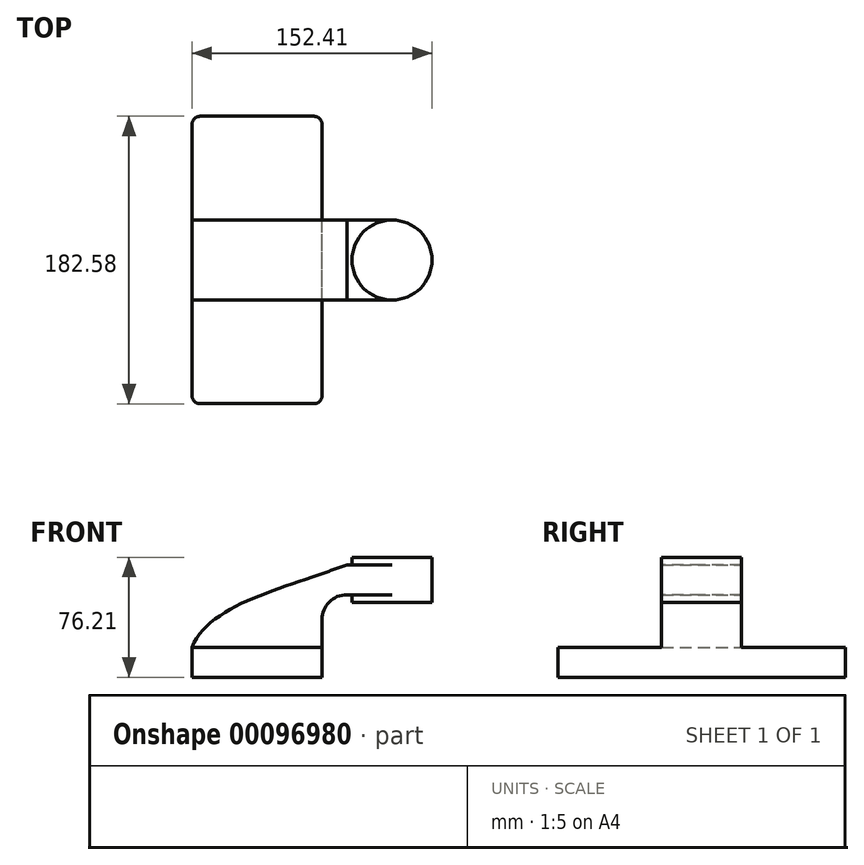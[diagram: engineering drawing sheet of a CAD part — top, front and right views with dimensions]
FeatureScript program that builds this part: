
annotation { "Feature Type Name" : "Feature", "Feature Type Description" : "" }
export const myFeature = defineFeature(function(context is Context, id is Id, definition is map)
    precondition{}
    {
        {
            var Q0;
            Q0=qCreatedBy(makeId("Front.planeOp"),FACE);
            var sketch = newSketch(context, id + "F0", { "sketchPlane" : qUnion([Q0])});
            skLineSegment(sketch, "E0.rect.bottom", {"start": v(-41.28, 9.53) * mm, "end": v(41.28, 9.53) * mm});
            skLineSegment(sketch, "E0.rect.top", {"start": v(-41.28, -9.53) * mm, "end": v(41.28, -9.53) * mm});
            skLineSegment(sketch, "E0.rect.left", {"start": v(-41.28, 9.52) * mm, "end": v(-41.28, -9.52) * mm});
            skLineSegment(sketch, "E0.rect.right", {"start": v(41.28, 9.52) * mm, "end": v(41.28, -9.52) * mm});
            skPoint(sketch, "E0.rect.middle", {"position": v(0, 0) * mm});
            skLineSegment(sketch, "E1", {"start": v(41.28, 9.52) * mm, "end": v(41.28, 27) * mm});
            skArc(sketch, "E2", {"start": v(41.28, 27) * mm, "mid": v(45.92, 38.23) * mm, "end": v(57.15, 42.88) * mm});
            skLineSegment(sketch, "E3", {"start": v(57.15, 42.88) * mm, "end": v(85.72, 42.88) * mm});
            skLineSegment(sketch, "E4.rect.bottom", {"start": v(60.32, 38.1) * mm, "end": v(111.12, 38.1) * mm});
            skLineSegment(sketch, "E4.rect.top", {"start": v(62.86, 66.67) * mm, "end": v(111.12, 66.67) * mm});
            skLineSegment(sketch, "E4.rect.left", {"start": v(60.32, 38.1) * mm, "end": v(60.32, 64.14) * mm});
            skLineSegment(sketch, "E4.rect.right", {"start": v(111.12, 38.1) * mm, "end": v(111.12, 66.68) * mm});
            skPoint(sketch, "E4.rect.middle", {"position": v(85.72, 52.39) * mm});
            skLineSegment(sketch, "E5.0", {"start": v(57.15, 61.93) * mm, "end": v(85.72, 61.93) * mm});
            skArc(sketch, "E5.1", {"start": v(22.23, 27) * mm, "mid": v(32.45, 51.7) * mm, "end": v(57.15, 61.93) * mm});
            skLineSegment(sketch, "E5.2", {"start": v(22.23, 9.53) * mm, "end": v(22.23, 27) * mm});
            skLineSegment(sketch, "E6", {"start": v(85.72, 38.1) * mm, "end": v(85.72, 66.68) * mm});
            skFitSpline(sketch, "E7", {"points": [v(-41.28, 9.52) * mm, v(57.15, 61.93) * mm], "startDerivative": vector(34.3, 84.37) * mm, "endDerivative": vector(112.4, 43.35) * mm});
            skPoint(sketch, "E8.visualSharp", {"position": v(60.32, 66.68) * mm});
            skArc(sketch, "E8.filletArc", {"start": v(62.86, 66.68) * mm, "mid": v(61.07, 65.93) * mm, "end": v(60.32, 64.14) * mm});
            skSolve(sketch);
        }
        {
            var Q0;
            Q0=makeQuery(id+"F0.imprint","IMPRINT",FACE,{"disambiguationData":[TD([[makeQuery(id+"F0.imprint","IMPRINT",EDGE,{"derivedFrom":sQuery(id+"F0.wireOp",EDGE,"E0.rect.top")}),1.0]])]});
            extrude(context, id + "F1", {"entities" : qUnion([Q0]), "endBound" : BoundingType.SYMMETRIC, "depth" : 182.57 * mm});
        }
        {
            var Q0;
            {var subQ9=sQuery(id+"F0.wireOp",EDGE,"E1");Q0=makeQuery(id+"F0.imprint","IMPRINT",FACE,{"disambiguationData":[TD([[makeQuery(id+"F0.imprint","IMPRINT",EDGE,{"derivedFrom":subQ9}),1.0]])]});}
            var Q1;
            {var subQ0=sQuery(id+"F0.wireOp",EDGE,"E6");var subQ1=sQuery(id+"F0.wireOp",EDGE,"E3");var subQ2=makeQuery(id+"F0.imprint","INTERSECT",VERTEX,{"derivedFrom":[subQ1,subQ0]});Q1=makeQuery(id+"F0.imprint","IMPRINT",FACE,{"disambiguationData":[TD([[makeQuery(id+"F0.imprint","IMPRINT",EDGE,{"disambiguationData":[TD([[subQ2,1.0]])],"derivedFrom":subQ1}),1.0]])]});}
            var Q2;
            {var subQ0=sQuery(id+"F0.wireOp",EDGE,"E7");var subQ1=sQuery(id+"F0.wireOp",EDGE,"E5.1");var subQ3=makeQuery(id+"F0.imprint","INTERSECT",VERTEX,{"derivedFrom":[subQ1,subQ0]});Q2=makeQuery(id+"F0.imprint","IMPRINT",FACE,{"disambiguationData":[TD([[makeQuery(id+"F0.imprint","IMPRINT",EDGE,{"disambiguationData":[TD([[subQ3,-1.0]])],"derivedFrom":subQ1}),-1.0]])]});}
            extrude(context, id + "F2", {"entities" : qUnion([Q0, Q1, Q2]), "operationType" : NewBodyOperationType.ADD, "endBound" : BoundingType.SYMMETRIC, "depth" : 50.8 * mm});
        }
        {
            var Q0;
            {var subQ3=sQuery(id+"F0.wireOp",EDGE,"E5.2");Q0=makeQuery(id+"F0.imprint","IMPRINT",FACE,{"disambiguationData":[TD([[makeQuery(id+"F0.imprint","IMPRINT",EDGE,{"derivedFrom":subQ3}),1.0]])]});}
            var Q1;
            {var subQ9=sQuery(id+"F0.wireOp",EDGE,"E1");Q1=makeQuery(id+"F0.imprint","IMPRINT",FACE,{"disambiguationData":[TD([[makeQuery(id+"F0.imprint","IMPRINT",EDGE,{"derivedFrom":subQ9}),1.0]])]});}
            extrude(context, id + "F3", {"entities" : qUnion([Q0, Q1]), "operationType" : NewBodyOperationType.ADD, "endBound" : BoundingType.SYMMETRIC, "depth" : 15.88 * mm});
        }
        {
            var Q0;
            {var subQ5=sQuery(id+"F0.wireOp",EDGE,"E4.rect.right");Q0=makeQuery(id+"F0.imprint","IMPRINT",FACE,{"disambiguationData":[TD([[makeQuery(id+"F0.imprint","IMPRINT",EDGE,{"derivedFrom":subQ5}),1.0]])]});}
            var Q1;
            Q1=sQuery(id+"F0.wireOp",EDGE,"E6");
            revolve(context, id + "F4", {"operationType" : NewBodyOperationType.ADD, "entities" : qUnion([Q0]), "axis" : qUnion([Q1]), "revolveType" : RevolveType.FULL});
        }
        {
            var Q0;
            Q0=makeQuery(id+"F1.opExtrude","CAP_EDGE",EDGE,{"disambiguationData":[OSD([sQuery(id+"F0.wireOp",EDGE,"E0.rect.right")])],"isStart":false});
            var Q1;
            Q1=makeQuery(id+"F1.opExtrude","CAP_EDGE",EDGE,{"disambiguationData":[OSD([sQuery(id+"F0.wireOp",EDGE,"E0.rect.left")])],"isStart":false});
            var Q2;
            Q2=makeQuery(id+"F1.opExtrude","CAP_EDGE",EDGE,{"disambiguationData":[OSD([sQuery(id+"F0.wireOp",EDGE,"E0.rect.right")])],"isStart":true});
            var Q3;
            Q3=makeQuery(id+"F1.opExtrude","CAP_EDGE",EDGE,{"disambiguationData":[OSD([sQuery(id+"F0.wireOp",EDGE,"E0.rect.left")])],"isStart":true});
            fillet(context, id + "F5", {"entities" : qUnion([Q0, Q1, Q2, Q3]), "radius" : 5.08 * mm, "tangentPropagation" : true, "allowEdgeOverflow" : false});
        }
    });
